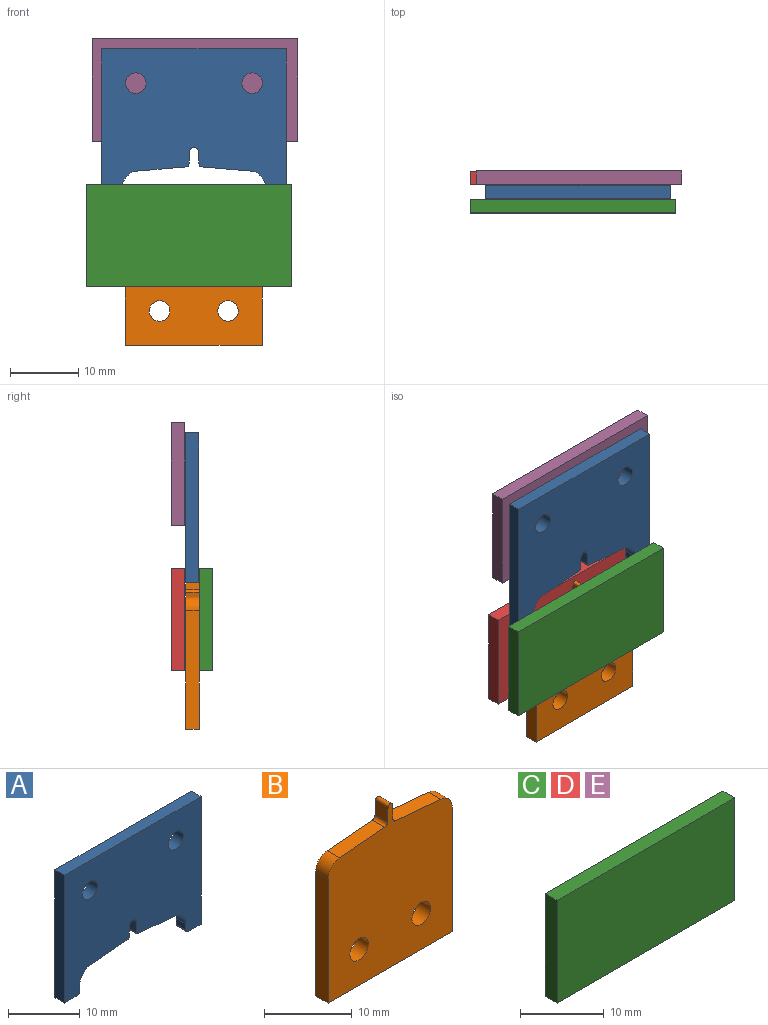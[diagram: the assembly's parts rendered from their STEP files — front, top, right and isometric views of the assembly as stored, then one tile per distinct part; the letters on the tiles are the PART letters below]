
ASSEMBLY  parts=5 mates=2
PART A: 22 faces, bbox 27x1.9x21.8 mm
  f0: plane 27x1.9mm, normal (0,0,1), area 51.3mm2, adj f1,f18,f20,f21
  f1: plane 21.84x1.9mm, normal (-1,0,0), area 41.5mm2, adj f0,f2,f20,f21
  f2: plane 2.5x1.9mm, normal (0,0,-1), area 4.8mm2, adj f1,f3,f20,f21
  f3: cylinder r=0.5mm len=1.9mm, axis (0,1,0), area 1.5mm2, adj f2,f4,f20,f21
  f4: plane 1.9x1mm, normal (1,0,0), area 1.9mm2, adj f3,f5,f20,f21
  f5: cylinder r=2.5mm len=2.49mm, axis (0,1,0), area 7mm2, adj f4,f6,f20,f21
  f6: plane 7.25x1.9mm, normal (0.09,0,-1), area 13.8mm2, adj f5,f7,f20,f21
  f7: cylinder r=0.25mm len=1.9mm, axis (0,1,0), area 0.7mm2, adj f6,f8,f20,f21
  f8: plane 1.96x1.9mm, normal (1,0,-0.05), area 3.7mm2, adj f7,f9,f20,f21
  f9: cylinder r=0.65mm len=1.9mm, axis (0,1,0), area 3.8mm2, adj f8,f10,f20,f21
  f10: plane 1.96x1.9mm, normal (-1,0,-0.05), area 3.7mm2, adj f9,f11,f20,f21
  f11: cylinder r=0.25mm len=1.9mm, axis (0,1,0), area 0.7mm2, adj f10,f12,f20,f21
  f12: plane 7.25x1.9mm, normal (-0.09,0,-1), area 13.8mm2, adj f11,f13,f20,f21
  f13: cylinder r=2.5mm len=2.49mm, axis (0,1,0), area 7mm2, adj f12,f14,f20,f21
  f14: plane 1.9x1mm, normal (-1,0,0), area 1.9mm2, adj f13,f15,f20,f21
  f15: cylinder r=0.5mm len=1.9mm, axis (0,1,0), area 1.5mm2, adj f14,f16,f20,f21
  f16: plane 2.5x1.9mm, normal (0,0,-1), area 4.8mm2, adj f15,f18,f20,f21
  f17: cylinder r=1.5mm len=3mm, axis (0,1,0), area 17.9mm2, adj f20,f21
  f18: plane 21.84x1.9mm, normal (1,0,0), area 41.5mm2, adj f0,f16,f20,f21
  f19: cylinder r=1.5mm len=3mm, axis (0,1,0), area 17.9mm2, adj f20,f21
  f20: plane 27x21.84mm, normal (0,-1,0), area 484.6mm2, adj f0,f1,f2,f3,f4,f5,f6,f7
  f21: plane 27x21.84mm, normal (0,1,0), area 484.6mm2, adj f0,f1,f2,f3,f4,f5,f6,f7
PART B: 16 faces, bbox 20x2x22.8 mm
  f0: plane 17.33x2mm, normal (-1,0,0), area 34.7mm2, adj f1,f12,f14,f15
  f1: plane 20x2mm, normal (0,0,-1), area 40mm2, adj f0,f2,f14,f15
  f2: plane 17.33x2mm, normal (1,0,0), area 34.7mm2, adj f1,f3,f14,f15
  f3: cylinder r=2mm len=2mm, axis (0,1,0), area 5.9mm2, adj f2,f4,f14,f15
  f4: plane 7.29x2mm, normal (0.09,0,1), area 14.6mm2, adj f3,f5,f14,f15
  f5: cylinder r=0.5mm len=2mm, axis (0,1,0), area 1.4mm2, adj f4,f6,f14,f15
  f6: plane 2.02x2mm, normal (1,0,0.04), area 4.1mm2, adj f5,f7,f14,f15
  f7: cylinder r=0.35mm len=2mm, axis (0,1,0), area 2.1mm2, adj f6,f8,f14,f15
  f8: plane 2.02x2mm, normal (-1,0,0.04), area 4.1mm2, adj f7,f9,f14,f15
  f9: cylinder r=0.5mm len=2mm, axis (0,1,0), area 1.4mm2, adj f8,f10,f14,f15
  f10: plane 7.29x2mm, normal (-0.09,0,1), area 14.6mm2, adj f9,f12,f14,f15
  f11: cylinder r=1.5mm len=3mm, axis (0,1,0), area 18.8mm2, adj f14,f15
  f12: cylinder r=2mm len=2mm, axis (0,1,0), area 5.9mm2, adj f0,f10,f14,f15
  f13: cylinder r=1.5mm len=3mm, axis (0,1,0), area 18.8mm2, adj f14,f15
  f14: plane 22.8x20mm, normal (0,-1,0), area 378.7mm2, adj f0,f1,f2,f3,f4,f5,f6,f7
  f15: plane 22.8x20mm, normal (0,1,0), area 378.7mm2, adj f0,f1,f2,f3,f4,f5,f6,f7
PART C: 6 faces, bbox 30x2x15 mm
  f0: plane 15x2mm, normal (1,0,0), area 30mm2, adj f1,f3,f4,f5
  f1: plane 30x2mm, normal (0,0,1), area 60mm2, adj f0,f2,f4,f5
  f2: plane 15x2mm, normal (-1,0,0), area 30mm2, adj f1,f3,f4,f5
  f3: plane 30x2mm, normal (0,0,-1), area 60mm2, adj f0,f2,f4,f5
  f4: plane 30x15mm, normal (0,-1,0), area 450mm2, adj f0,f1,f2,f3
  f5: plane 30x15mm, normal (0,1,0), area 450mm2, adj f0,f1,f2,f3
PART D: same geometry as C
PART E: same geometry as C
PLACE A t=(1.59,5.6,-12.5)mm
PLACE B t=(1.57,5.6,-12.8)mm
PLACE C t=(0.9,3.6,-11.77)mm
PLACE D t=(0.88,7.73,-11.74)mm
PLACE E t=(1.72,7.72,9.49)mm
MATE planar B.f14 <-> C.f5  axis (0,-1,0) through (1.57,3.6,-17.78)mm
MATE planar A.f21 <-> B.f15  axis (0,1,0) through (1.59,5.6,6.03)mm
